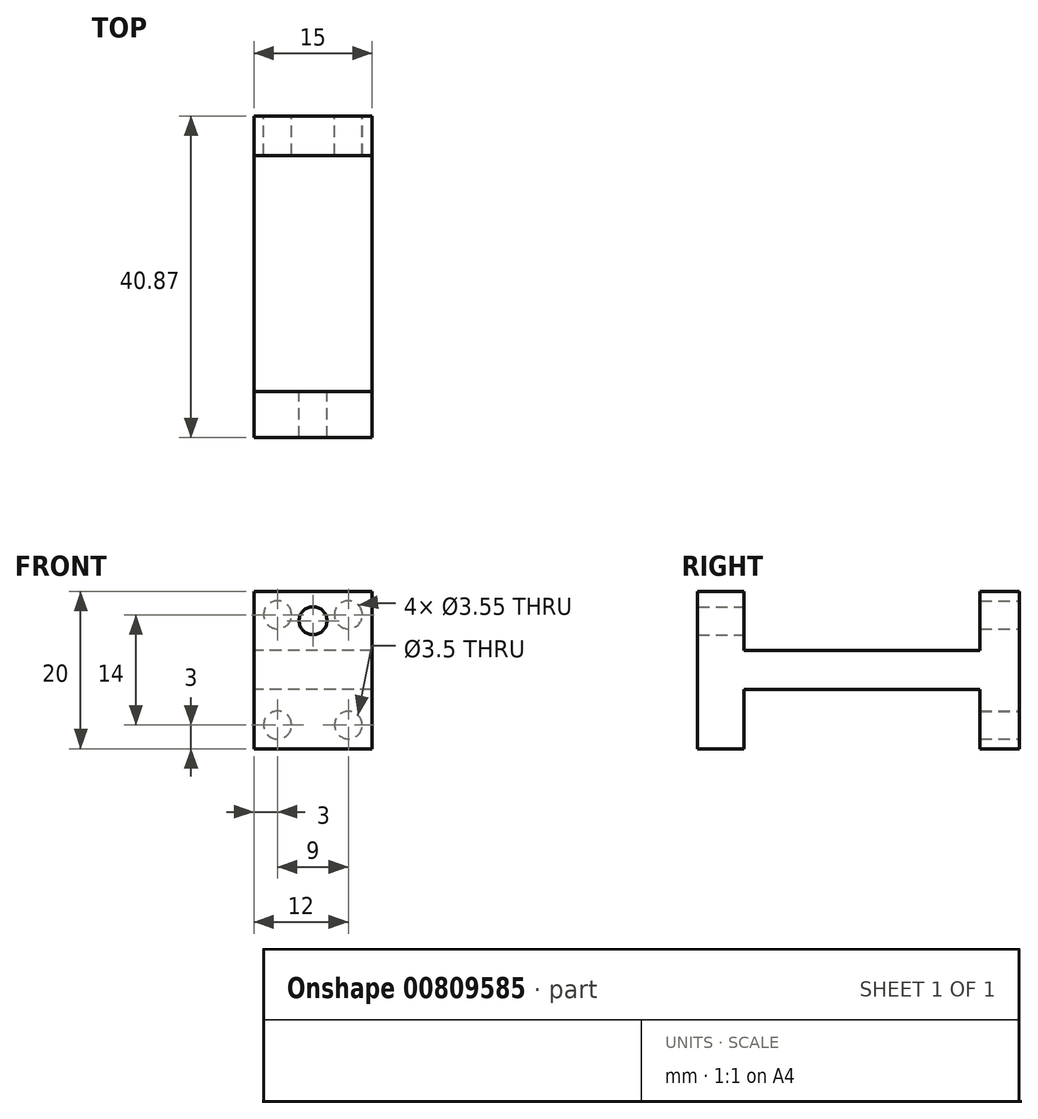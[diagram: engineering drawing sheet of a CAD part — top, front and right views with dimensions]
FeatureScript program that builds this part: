
annotation { "Feature Type Name" : "Feature", "Feature Type Description" : "" }
export const myFeature = defineFeature(function(context is Context, id is Id, definition is map)
    precondition{}
    {
        {
            var Q0;
            Q0=qCreatedBy(makeId("Right.planeOp"),FACE);
            var sketch = newSketch(context, id + "F0", { "sketchPlane" : qUnion([Q0])});
            skLineSegment(sketch, "E0.bottom", {"start": v(-14, 10) * mm, "end": v(-8.13, 10) * mm});
            skLineSegment(sketch, "E0.top", {"start": v(-14, -10) * mm, "end": v(-8.13, -10) * mm});
            skLineSegment(sketch, "E0.left", {"start": v(-14, 10) * mm, "end": v(-14, -10) * mm});
            skLineSegment(sketch, "E0.right", {"start": v(-8.13, 10) * mm, "end": v(-8.13, -10) * mm});
            skLineSegment(sketch, "E1.bottom", {"start": v(-8.13, 2.5) * mm, "end": v(21.87, 2.5) * mm});
            skLineSegment(sketch, "E1.top", {"start": v(-8.13, -2.5) * mm, "end": v(21.87, -2.5) * mm});
            skLineSegment(sketch, "E1.left", {"start": v(-8.13, 2.5) * mm, "end": v(-8.13, -2.5) * mm});
            skLineSegment(sketch, "E1.right", {"start": v(21.87, 2.5) * mm, "end": v(21.87, -2.5) * mm});
            skLineSegment(sketch, "E2.bottom", {"start": v(21.87, 10) * mm, "end": v(26.87, 10) * mm});
            skLineSegment(sketch, "E2.top", {"start": v(21.87, -10) * mm, "end": v(26.87, -10) * mm});
            skLineSegment(sketch, "E2.left", {"start": v(21.87, 10) * mm, "end": v(21.87, -10) * mm});
            skLineSegment(sketch, "E2.right", {"start": v(26.87, 10) * mm, "end": v(26.87, -10) * mm});
            skSolve(sketch);
        }
        {
            var Q0;
            Q0 = qSketchRegion(id + "F0", true);
            extrude(context, id + "F1", {"entities" : qUnion([Q0]), "depth" : 15 * mm, "offsetDistance" : 25 * mm});
        }
        {
            var Q0;
            Q0=makeQuery(id+"F1.opExtrude","SWEPT_FACE",FACE,{"disambiguationData":[OSD([sQuery(id+"F0.wireOp",EDGE,"E2.right")])]});
            var sketch = newSketch(context, id + "F2", { "sketchPlane" : qUnion([Q0])});
            skCircle(sketch, "E3", {"center": v(-12, 7) * mm, "radius": 1.78 * mm});
            skCircle(sketch, "E4", {"center": v(-3, 7) * mm, "radius": 1.77 * mm});
            skCircle(sketch, "E5", {"center": v(-3, -7) * mm, "radius": 1.77 * mm});
            skCircle(sketch, "E6", {"center": v(-12, -7) * mm, "radius": 1.75 * mm});
            skSolve(sketch);
        }
        {
            var Q0;
            {var subQ0=sQuery(id+"F0.wireOp",EDGE,"E0.right");Q0=makeQuery(id+"F1.opExtrude","SWEPT_FACE",FACE,{"disambiguationData":[OSD([subQ0]),TDD([makeQuery(id+"F0.imprint","IMPRINT",EDGE,{"disambiguationData":[TD([[makeQuery(id+"F0.imprint","INTERSECT",VERTEX,{"derivedFrom":[sQuery(id+"F0.wireOp",EDGE,"E0.bottom"),subQ0]}),-1.0]])],"derivedFrom":subQ0})])]});}
            var sketch = newSketch(context, id + "F3", { "sketchPlane" : qUnion([Q0])});
            skCircle(sketch, "E7", {"center": v(-7.5, 6.25) * mm, "radius": 1.77 * mm});
            skSolve(sketch);
        }
        {
            var Q0;
            Q0 = qSketchRegion(id + "F3", true);
            extrude(context, id + "F4", {"entities" : qUnion([Q0]), "operationType" : NewBodyOperationType.REMOVE, "oppositeDirection" : true, "depth" : 25 * mm, "offsetDistance" : 25 * mm});
        }
        {
            var Q0;
            Q0 = qSketchRegion(id + "F2", true);
            extrude(context, id + "F5", {"entities" : qUnion([Q0]), "operationType" : NewBodyOperationType.REMOVE, "oppositeDirection" : true, "depth" : 25 * mm, "offsetDistance" : 25 * mm});
        }
    });
